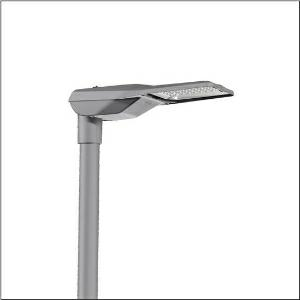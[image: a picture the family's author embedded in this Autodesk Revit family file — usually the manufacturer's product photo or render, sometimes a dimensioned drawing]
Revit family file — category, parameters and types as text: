
# Revit family: streetlight_sl_21_mini___st1_5a_5xe2p33s08gb_ee16
name_source: partatom
category: Lighting Fixtures
units: mm (PartAtom-declared; Revit-internal decimal feet)

## family parameters
Cut with Voids When Loaded = No
Host = Face
Light Source = No
Part Type = Normal
Room Calculation Point = No
Round Connector Dimension = Use Diameter
Shared = No

## types (1)
- --- (1 x LED, 5840 lm, 40.4 W, 3000K)
    Apparent Load = 40 VA
    CIE Flux Codes = 22 53 95 100 100
    Color Rendering = 70
    Color Temperature = 3000K
    Default Elevation = 1800 mm
    Description = Streetlight SL 21 mini, mast luminaire, primary light control with lens, of PMMA, primary optical cover: cover, of toughened safety glass, transparent, light distribution: ST1.5a, light emission: direct distribution, primary light characteristic: asymmetric, installation type: side-entry, post-top, LED, High Power LED, rated luminous flux: 5.840lm, luminous efficacy: 144lm/W, light colour: 730, colour temperature: 3000K, control gear: ECG Smart Interface, control: overheat protection, constant luminous flux control, time-dependent luminous flux control, flexible luminous flux parameterisation, mains connection: 220..240V, AC, 50/60Hz, start of lifetime: 40W, end of lifetime: 41W, reduction: 19W, luminaire housing, of diecast aluminium, powder-coated, Siteco® metallic grey (DB 702S), corrosivity category C5 according to DIN EN ISO 12944, length: 628mm, width: 235mm, height: 110mm, spigot size: 60/76mm (post-top) and 42/60/76mm (side-entry), mast flange for spigot size: 42mm: 5XC10008XM4, 60mm: 5XC10008XM2, 76/60mm: 5XC10108XM1, protection rating (complete): IP66, insulation class (complete): insulation class II (safety insulation), certification: CE, ENEC, VDE, impact resistance: IK09, permissible operating ambient temperature for outdoor applications: -40..+50°C, standard-compliant lighting for roads and squares, packaging unit: 1 piece

Light Distribution: ST1.5a
    Height = 110 mm
    Lamp = 1 x LED
    Lamp Light Flux = 5840 lm
    Lamp Power = 40.4 W
    Lamp count = 1
    Length = 625 mm
    Luminous efficacy = 145 lm/W
    Manufacturer = Siteco
    ModVariant = No
    Model = 5XE2P33S08GB
    Number of Poles = 1
    OnlyDefault = Yes
    Power Factor = 1
    Product Name = Streetlight SL 21 mini | ST1.5a
    Product group = mast luminaire | pylon top
    ProductGroupID = 6100
    Protection Class = Protection class II
    Protection Degree = IP 66
    RLX_Detail_Level = 1
    RlxData = <blob elided: 95489 chars, md5=8aeafc3d>
    Socket = socket
    Standby Power = 0 W
    System Light Flux = 5840 lm
    System Power = 40 W
    Type Comments = factory setting: luminous flux: 100 % | dim-lin: 254 | 812 mA
    Type Image = l_1003515.jpg
    URL = http://relux.com
    VarID = @adj_088523
    Voltage = 0 V
    Weight = 0.00 kg
    Width = 234 mm

## geometry (parser evidence)
native form markers: Blend x4, Sweep x7
no freeform markers — native parametric forms only
